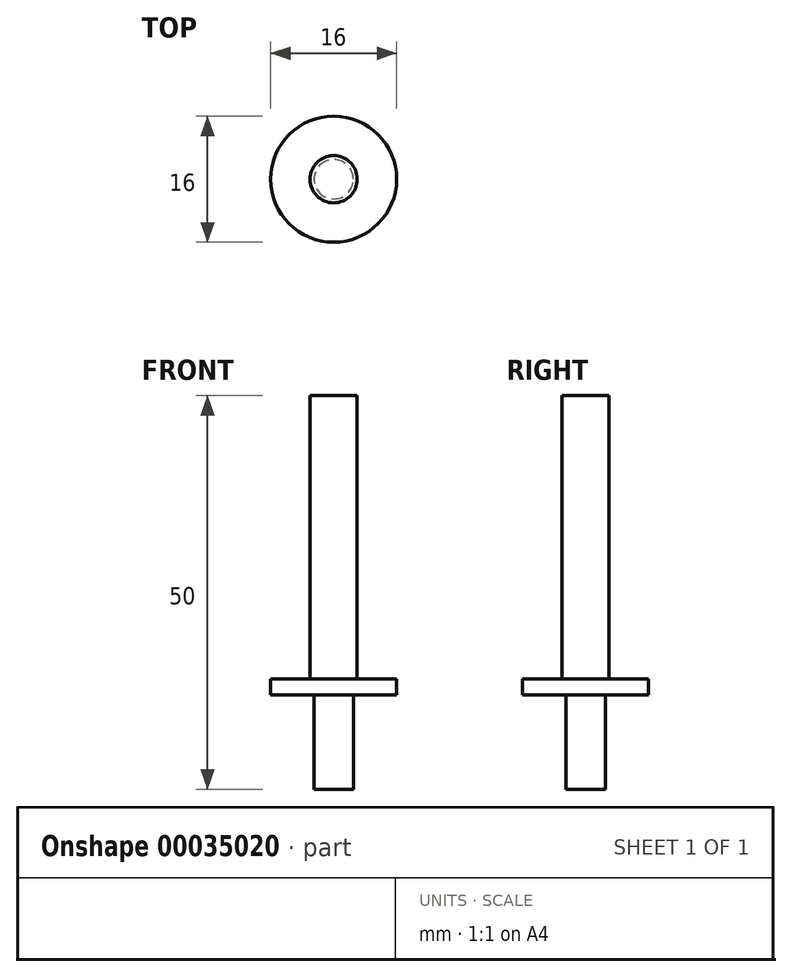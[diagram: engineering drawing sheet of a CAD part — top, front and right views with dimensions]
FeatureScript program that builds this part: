
annotation { "Feature Type Name" : "Feature", "Feature Type Description" : "" }
export const myFeature = defineFeature(function(context is Context, id is Id, definition is map)
    precondition{}
    {
        {
            var Q0;
            Q0=qCreatedBy(makeId("Top.planeOp"),FACE);
            var sketch = newSketch(context, id + "F0", { "sketchPlane" : qUnion([Q0])});
            skCircle(sketch, "E0", {"center": v(0, 0) * mm, "radius": 2.5 * mm});
            skSolve(sketch);
        }
        {
            var Q0;
            Q0 = qSketchRegion(id + "F0", true);
            var Q1;
            Q1=makeQuery(id+"F0.imprint","IMPRINT",FACE,{"disambiguationData":[TD([[makeQuery(id+"F0.imprint","IMPRINT",EDGE,{"derivedFrom":sQuery(id+"F0.wireOp",EDGE,"E0")}),1.0]])]});
            extrude(context, id + "F1", {"entities" : qUnion([Q0, Q1]), "depth" : 12 * mm});
        }
        {
            var Q0;
            Q0=makeQuery(id+"F1.opExtrude","CAP_FACE",FACE,{"disambiguationData":[OSD([sQuery(id+"F0.wireOp",EDGE,"E0")])],"isStart":false});
            var sketch = newSketch(context, id + "F2", { "sketchPlane" : qUnion([Q0])});
            skCircle(sketch, "E1", {"center": v(0, 0) * mm, "radius": 8 * mm});
            skSolve(sketch);
        }
        {
            var Q0;
            Q0 = qSketchRegion(id + "F2", true);
            var Q1;
            Q1=makeQuery(id+"F2.imprint","IMPRINT",FACE,{"disambiguationData":[TD([[makeQuery(id+"F2.imprint","IMPRINT",EDGE,{"derivedFrom":sQuery(id+"F2.wireOp",EDGE,"E1")}),1.0]])]});
            extrude(context, id + "F3", {"entities" : qUnion([Q0, Q1]), "operationType" : NewBodyOperationType.ADD, "depth" : 2 * mm});
        }
        {
            var Q0;
            Q0=makeQuery(id+"F3.opExtrude","CAP_FACE",FACE,{"disambiguationData":[OSD([sQuery(id+"F2.wireOp",EDGE,"E1")])],"isStart":false});
            var sketch = newSketch(context, id + "F4", { "sketchPlane" : qUnion([Q0])});
            skCircle(sketch, "E2", {"center": v(0, 0) * mm, "radius": 3 * mm});
            skSolve(sketch);
        }
        {
            var Q0;
            Q0 = qSketchRegion(id + "F4", true);
            var Q1;
            Q1=makeQuery(id+"F4.imprint","IMPRINT",FACE,{"disambiguationData":[TD([[makeQuery(id+"F4.imprint","IMPRINT",EDGE,{"derivedFrom":sQuery(id+"F4.wireOp",EDGE,"E2")}),1.0]])]});
            extrude(context, id + "F5", {"entities" : qUnion([Q0, Q1]), "operationType" : NewBodyOperationType.ADD, "depth" : 36 * mm});
        }
    });
